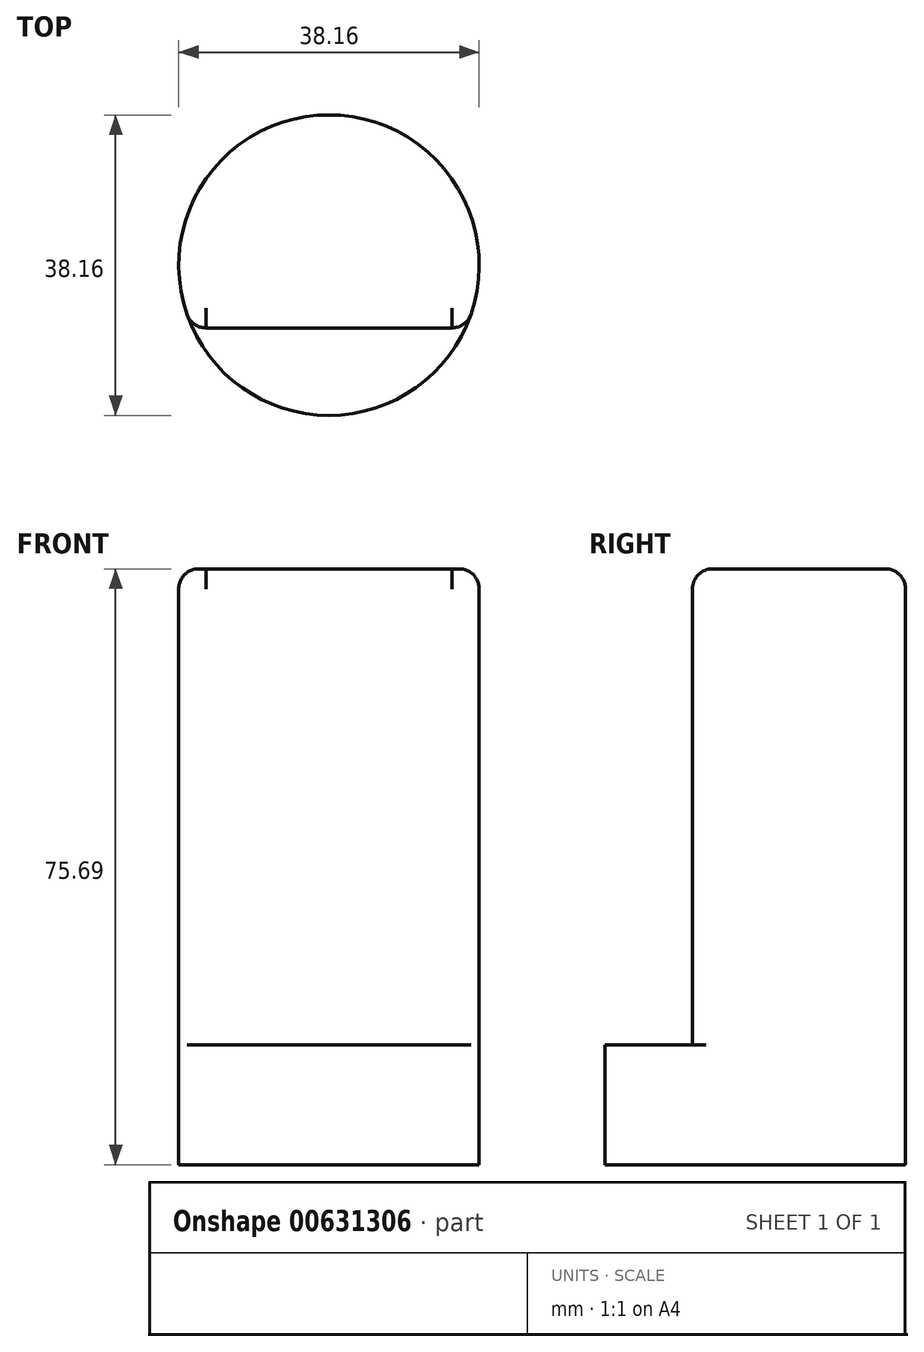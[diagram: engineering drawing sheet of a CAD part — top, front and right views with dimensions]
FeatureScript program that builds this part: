
annotation { "Feature Type Name" : "Feature", "Feature Type Description" : "" }
export const myFeature = defineFeature(function(context is Context, id is Id, definition is map)
    precondition{}
    {
        {
            var Q0;
            Q0=qCreatedBy(makeId("Top.planeOp"),FACE);
            var sketch = newSketch(context, id + "F0", { "sketchPlane" : qUnion([Q0])});
            skCircle(sketch, "E0", {"center": v(0, 0) * mm, "radius": 19.08 * mm});
            skSolve(sketch);
        }
        {
            var Q0;
            Q0=makeQuery(id+"F0.imprint","IMPRINT",FACE,{"disambiguationData":[TD([[makeQuery(id+"F0.imprint","IMPRINT",EDGE,{"derivedFrom":sQuery(id+"F0.wireOp",EDGE,"E0")}),1.0]])]});
            var Q1;
            Q1=sQuery(id+"F0.wireOp",EDGE,"E0");
            extrude(context, id + "F1", {"entities" : qUnion([Q0]), "surfaceEntities" : qUnion([Q1]), "depth" : 15.24 * mm, "offsetDistance" : 25.4 * mm});
        }
        {
            var Q0;
            Q0=makeQuery(id+"F1.opExtrude","CAP_FACE",FACE,{"disambiguationData":[OSD([sQuery(id+"F0.wireOp",EDGE,"E0")])],"isStart":false});
            var sketch = newSketch(context, id + "F2", { "sketchPlane" : qUnion([Q0])});
            skArc(sketch, "E1.0", {"start": v(17.34, -7.97) * mm, "mid": v(0, 19.08) * mm, "end": v(-17.34, -7.97) * mm});
            skLineSegment(sketch, "E2", {"start": v(-17.34, -7.97) * mm, "end": v(17.34, -7.97) * mm});
            skSolve(sketch);
        }
        {
            var Q0;
            Q0 = qSketchRegion(id + "F2", true);
            extrude(context, id + "F3", {"entities" : qUnion([Q0]), "operationType" : NewBodyOperationType.ADD, "depth" : 60.45 * mm, "offsetDistance" : 25.4 * mm});
        }
        {
            var Q0;
            Q0=makeQuery(id+"F3.opExtrude","CAP_EDGE",EDGE,{"disambiguationData":[OSD([sQuery(id+"F2.wireOp",EDGE,"E2")])],"isStart":true});
            var Q1;
            Q1=makeQuery(id+"F3.opExtrude","CAP_EDGE",EDGE,{"disambiguationData":[OSD([sQuery(id+"F2.wireOp",EDGE,"E2")])],"isStart":false});
            fillet(context, id + "F4", {"entities" : qUnion([Q0, Q1]), "radius" : 2.54 * mm, "tangentPropagation" : true, "allowEdgeOverflow" : false});
        }
        {
            var Q0;
            {var subQ0=sQuery(id+"F2.wireOp",EDGE,"E2");var subQ1=sQuery(id+"F2.wireOp",EDGE,"E1.0");var subQ2=sQuery(id+"F0.wireOp",EDGE,"E0");Q0=makeQuery(id+"F3.opExtrude","SWEPT_EDGE",EDGE,{"disambiguationData":[OSD([subQ2,subQ1,subQ0]),TDD([makeQuery(id+"F2.imprint","INTERSECT",VERTEX,{"disambiguationData":[OD(0.0)],"derivedFrom":[makeQuery(id+"F1.opExtrude","CAP_EDGE",EDGE,{"disambiguationData":[OSD([subQ2])],"isStart":false}),subQ1,subQ0]})])]});}
            fillet(context, id + "F5", {"entities" : qUnion([Q0]), "radius" : 2.54 * mm, "tangentPropagation" : true, "allowEdgeOverflow" : false});
        }
    });
